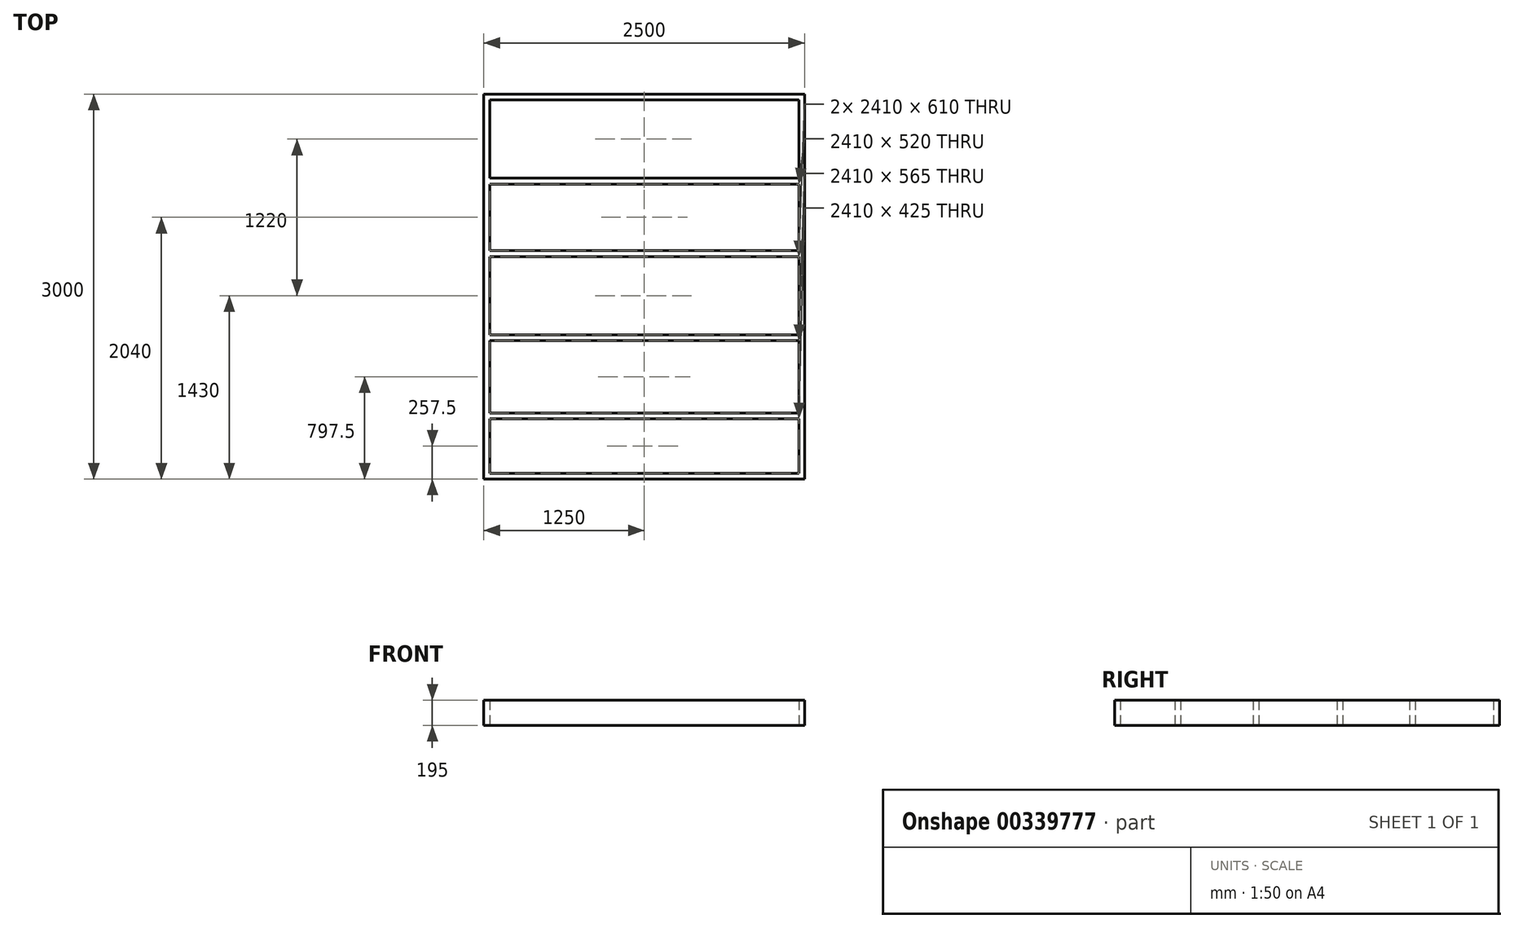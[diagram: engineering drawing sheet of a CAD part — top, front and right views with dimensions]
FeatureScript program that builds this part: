
annotation { "Feature Type Name" : "Feature", "Feature Type Description" : "" }
export const myFeature = defineFeature(function(context is Context, id is Id, definition is map)
    precondition{}
    {
        {
            var Q0;
            Q0=qCreatedBy(makeId("Top.planeOp"),FACE);
            var sketch = newSketch(context, id + "F0", { "sketchPlane" : qUnion([Q0])});
            skLineSegment(sketch, "E0.bottom", {"start": v(0, 0) * mm, "end": v(2500, 0) * mm});
            skLineSegment(sketch, "E0.top", {"start": v(0, 3000) * mm, "end": v(2500, 3000) * mm});
            skLineSegment(sketch, "E1.0", {"start": v(45, 2955) * mm, "end": v(2455, 2955) * mm});
            skLineSegment(sketch, "E1.1", {"start": v(45, 45) * mm, "end": v(45, 470) * mm});
            skLineSegment(sketch, "E1.2", {"start": v(45, 45) * mm, "end": v(2455, 45) * mm});
            skLineSegment(sketch, "E1.3", {"start": v(2455, 45) * mm, "end": v(2455, 470) * mm});
            skLineSegment(sketch, "E2", {"start": v(45, 2345) * mm, "end": v(2455, 2345) * mm});
            skLineSegment(sketch, "E3", {"start": v(2455, 1780) * mm, "end": v(45, 1780) * mm});
            skLineSegment(sketch, "E4", {"start": v(45, 1125) * mm, "end": v(2455, 1125) * mm});
            skLineSegment(sketch, "E5", {"start": v(2455, 515) * mm, "end": v(45, 515) * mm});
            skLineSegment(sketch, "E6", {"start": v(2500, 3000) * mm, "end": v(2500, 0) * mm});
            skLineSegment(sketch, "E7", {"start": v(0, 0) * mm, "end": v(0, 3000) * mm});
            skLineSegment(sketch, "E8.0", {"start": v(45, 2300) * mm, "end": v(2455, 2300) * mm});
            skLineSegment(sketch, "E9.0", {"start": v(2455, 1735) * mm, "end": v(45, 1735) * mm});
            skLineSegment(sketch, "E10.0", {"start": v(45, 1080) * mm, "end": v(2455, 1080) * mm});
            skLineSegment(sketch, "E11.0", {"start": v(2455, 470) * mm, "end": v(45, 470) * mm});
            skLineSegment(sketch, "E12.trimOffspring", {"start": v(45, 2345) * mm, "end": v(45, 2955) * mm});
            skLineSegment(sketch, "E13.trimOffspring", {"start": v(2455, 2345) * mm, "end": v(2455, 2955) * mm});
            skPoint(sketch, "E14.orphan", {"position": v(2500, 2345) * mm});
            skLineSegment(sketch, "E15.trimOffspring", {"start": v(2455, 1780) * mm, "end": v(2455, 2300) * mm});
            skLineSegment(sketch, "E16.trimOffspring", {"start": v(45, 1780) * mm, "end": v(45, 2300) * mm});
            skPoint(sketch, "E17.orphan", {"position": v(0, 1780) * mm});
            skLineSegment(sketch, "E18.trimOffspring", {"start": v(45, 1125) * mm, "end": v(45, 1735) * mm});
            skPoint(sketch, "E19.orphan", {"position": v(2500, 1125) * mm});
            skLineSegment(sketch, "E20.trimOffspring", {"start": v(2455, 1125) * mm, "end": v(2455, 1735) * mm});
            skLineSegment(sketch, "E21.trimOffspring", {"start": v(45, 515) * mm, "end": v(45, 1080) * mm});
            skLineSegment(sketch, "E22.trimOffspring", {"start": v(2455, 515) * mm, "end": v(2455, 1080) * mm});
            skSolve(sketch);
        }
        {
            var Q0;
            Q0=makeQuery(id+"F0.imprint","IMPRINT",FACE,{"disambiguationData":[TD([[makeQuery(id+"F0.imprint","IMPRINT",EDGE,{"derivedFrom":sQuery(id+"F0.wireOp",EDGE,"E0.bottom")}),1.0]])]});
            extrude(context, id + "F1", {"entities" : qUnion([Q0]), "depth" : 195 * mm});
        }
    });
